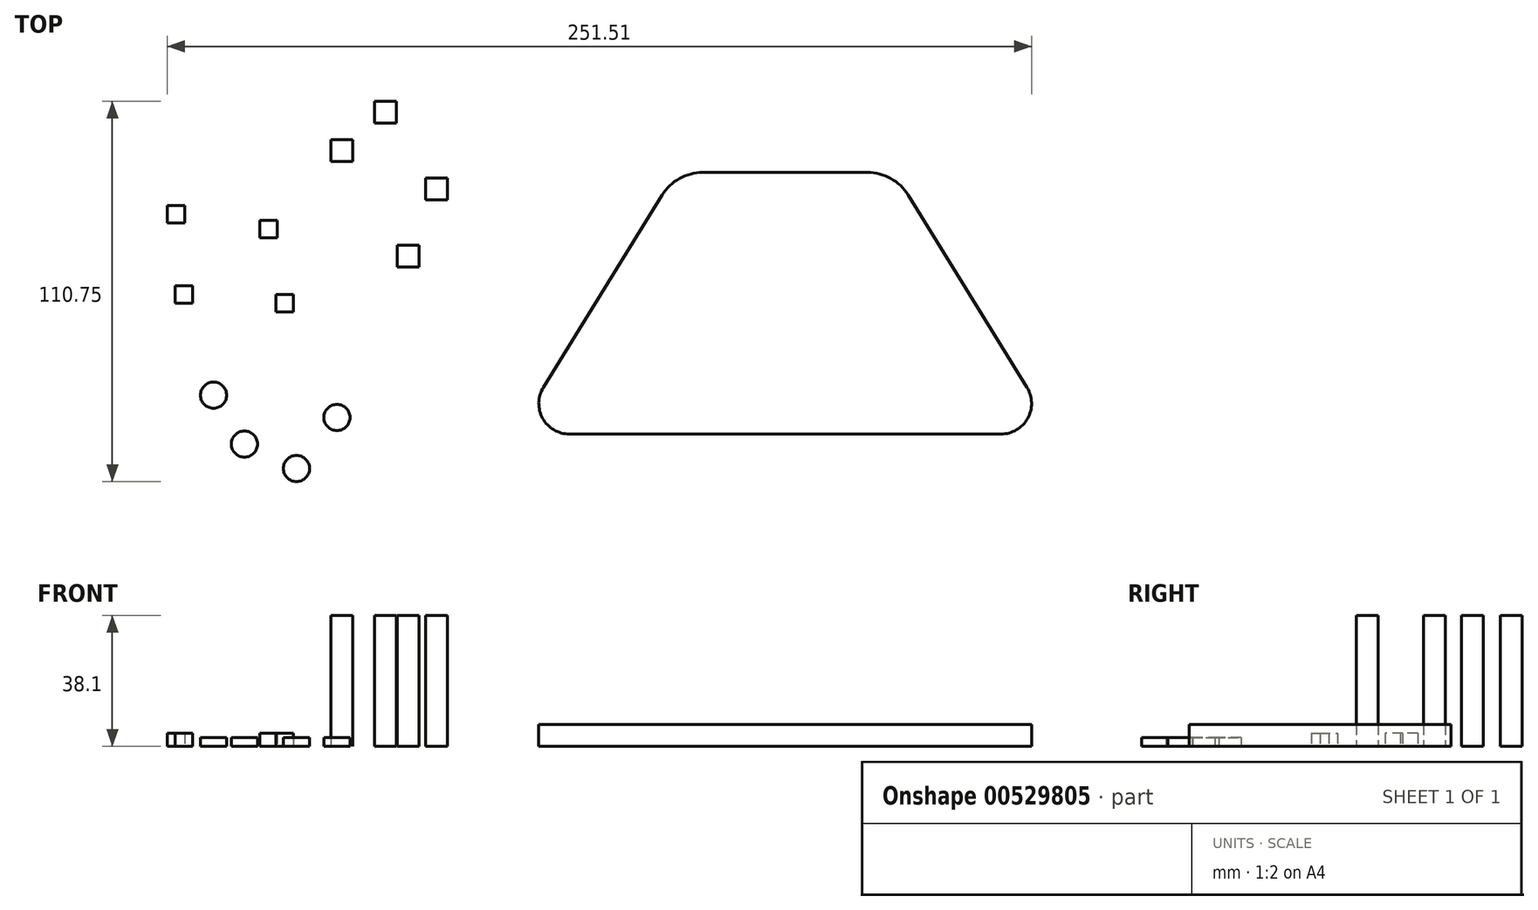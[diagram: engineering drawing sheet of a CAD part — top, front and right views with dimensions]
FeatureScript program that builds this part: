
annotation { "Feature Type Name" : "Feature", "Feature Type Description" : "" }
export const myFeature = defineFeature(function(context is Context, id is Id, definition is map)
    precondition{}
    {
        {
            var Q0;
            Q0=qCreatedBy(makeId("Top.planeOp"),FACE);
            var sketch = newSketch(context, id + "F0", { "sketchPlane" : qUnion([Q0])});
            skLineSegment(sketch, "E0.bottom", {"start": v(-23.95, 38.1) * mm, "end": v(23.95, 38.1) * mm});
            skLineSegment(sketch, "E0.top", {"start": v(-31.75, -38.1) * mm, "end": v(31.75, -38.1) * mm});
            skLineSegment(sketch, "E0.left", {"start": v(-31.75, 38.1) * mm, "end": v(-31.75, -38.1) * mm});
            skLineSegment(sketch, "E0.right", {"start": v(31.75, 38.1) * mm, "end": v(31.75, -38.1) * mm});
            skPoint(sketch, "E0.middle", {"position": v(0, 0) * mm});
            skLineSegment(sketch, "E1", {"start": v(-31.75, -38.1) * mm, "end": v(-62.81, -38.1) * mm});
            skLineSegment(sketch, "E2", {"start": v(31.75, -38.1) * mm, "end": v(62.81, -38.1) * mm});
            skLineSegment(sketch, "E3", {"start": v(-35.84, 31.46) * mm, "end": v(-70.38, -24.54) * mm});
            skLineSegment(sketch, "E4", {"start": v(35.84, 31.46) * mm, "end": v(70.38, -24.54) * mm});
            skPoint(sketch, "E5.visualSharp", {"position": v(-31.75, 38.1) * mm});
            skArc(sketch, "E5.filletArc", {"start": v(-23.95, 38.1) * mm, "mid": v(-30.76, 36.33) * mm, "end": v(-35.84, 31.46) * mm});
            skPoint(sketch, "E6.visualSharp", {"position": v(31.75, 38.1) * mm});
            skArc(sketch, "E6.filletArc", {"start": v(35.84, 31.46) * mm, "mid": v(30.76, 36.33) * mm, "end": v(23.95, 38.1) * mm});
            skPoint(sketch, "E7.visualSharp", {"position": v(-78.74, -38.1) * mm});
            skArc(sketch, "E7.filletArc", {"start": v(-70.38, -24.54) * mm, "mid": v(-70.58, -33.54) * mm, "end": v(-62.81, -38.1) * mm});
            skPoint(sketch, "E8.visualSharp", {"position": v(78.74, -38.1) * mm});
            skArc(sketch, "E8.filletArc", {"start": v(62.81, -38.1) * mm, "mid": v(70.58, -33.54) * mm, "end": v(70.38, -24.54) * mm});
            skSolve(sketch);
        }
        {
            var Q0;
            {var subQ4=sQuery(id+"F0.wireOp",EDGE,"E1");Q0=makeQuery(id+"F0.imprint","IMPRINT",FACE,{"disambiguationData":[TD([[makeQuery(id+"F0.imprint","IMPRINT",EDGE,{"derivedFrom":subQ4}),-1.0]])]});}
            var Q1;
            {var subQ7=sQuery(id+"F0.wireOp",EDGE,"E0.bottom");Q1=makeQuery(id+"F0.imprint","IMPRINT",FACE,{"disambiguationData":[TD([[makeQuery(id+"F0.imprint","IMPRINT",EDGE,{"derivedFrom":subQ7}),-1.0]])]});}
            var Q2;
            {var subQ4=sQuery(id+"F0.wireOp",EDGE,"E2");Q2=makeQuery(id+"F0.imprint","IMPRINT",FACE,{"disambiguationData":[TD([[makeQuery(id+"F0.imprint","IMPRINT",EDGE,{"derivedFrom":subQ4}),1.0]])]});}
            extrude(context, id + "F1", {"entities" : qUnion([Q0, Q1, Q2]), "depth" : 6.35 * mm, "offsetDistance" : 25.4 * mm});
        }
        {
            var Q0;
            Q0=qCreatedBy(makeId("Top.planeOp"),FACE);
            var sketch = newSketch(context, id + "F2", { "sketchPlane" : qUnion([Q0])});
            skLineSegment(sketch, "E9.bottom", {"start": v(-113.12, 52.46) * mm, "end": v(-119.47, 52.46) * mm});
            skLineSegment(sketch, "E9.top", {"start": v(-113.12, 58.81) * mm, "end": v(-119.47, 58.81) * mm});
            skLineSegment(sketch, "E9.left", {"start": v(-113.12, 52.46) * mm, "end": v(-113.12, 58.81) * mm});
            skLineSegment(sketch, "E9.right", {"start": v(-119.47, 52.46) * mm, "end": v(-119.47, 58.81) * mm});
            skPoint(sketch, "E9.middle", {"position": v(-116.3, 55.64) * mm});
            skLineSegment(sketch, "E10.bottom", {"start": v(-125.9, 41.24) * mm, "end": v(-132.24, 41.24) * mm});
            skLineSegment(sketch, "E10.top", {"start": v(-125.9, 47.6) * mm, "end": v(-132.24, 47.6) * mm});
            skLineSegment(sketch, "E10.left", {"start": v(-125.9, 41.24) * mm, "end": v(-125.9, 47.6) * mm});
            skLineSegment(sketch, "E10.right", {"start": v(-132.24, 41.24) * mm, "end": v(-132.24, 47.6) * mm});
            skPoint(sketch, "E10.middle", {"position": v(-129.07, 44.42) * mm});
            skLineSegment(sketch, "E11.bottom", {"start": v(-106.52, 10.57) * mm, "end": v(-112.87, 10.57) * mm});
            skLineSegment(sketch, "E11.top", {"start": v(-106.52, 16.92) * mm, "end": v(-112.87, 16.92) * mm});
            skLineSegment(sketch, "E11.left", {"start": v(-106.52, 10.57) * mm, "end": v(-106.52, 16.92) * mm});
            skLineSegment(sketch, "E11.right", {"start": v(-112.87, 10.57) * mm, "end": v(-112.87, 16.92) * mm});
            skPoint(sketch, "E11.middle", {"position": v(-109.7, 13.75) * mm});
            skLineSegment(sketch, "E12.bottom", {"start": v(-98.24, 30.1) * mm, "end": v(-104.6, 30.1) * mm});
            skLineSegment(sketch, "E12.top", {"start": v(-98.24, 36.44) * mm, "end": v(-104.6, 36.44) * mm});
            skLineSegment(sketch, "E12.left", {"start": v(-98.24, 30.1) * mm, "end": v(-98.24, 36.44) * mm});
            skLineSegment(sketch, "E12.right", {"start": v(-104.6, 30.1) * mm, "end": v(-104.6, 36.44) * mm});
            skPoint(sketch, "E12.middle", {"position": v(-101.42, 33.27) * mm});
            skSolve(sketch);
        }
        {
            var Q0;
            Q0=makeQuery(id+"F2.imprint","IMPRINT",FACE,{"disambiguationData":[TD([[makeQuery(id+"F2.imprint","IMPRINT",EDGE,{"derivedFrom":sQuery(id+"F2.wireOp",EDGE,"E9.bottom")}),-1.0]])]});
            var Q1;
            Q1=makeQuery(id+"F2.imprint","IMPRINT",FACE,{"disambiguationData":[TD([[makeQuery(id+"F2.imprint","IMPRINT",EDGE,{"derivedFrom":sQuery(id+"F2.wireOp",EDGE,"E11.bottom")}),-1.0]])]});
            var Q2;
            Q2=makeQuery(id+"F2.imprint","IMPRINT",FACE,{"disambiguationData":[TD([[makeQuery(id+"F2.imprint","IMPRINT",EDGE,{"derivedFrom":sQuery(id+"F2.wireOp",EDGE,"E12.bottom")}),-1.0]])]});
            var Q3;
            Q3=makeQuery(id+"F2.imprint","IMPRINT",FACE,{"disambiguationData":[TD([[makeQuery(id+"F2.imprint","IMPRINT",EDGE,{"derivedFrom":sQuery(id+"F2.wireOp",EDGE,"E10.bottom")}),-1.0]])]});
            extrude(context, id + "F3", {"entities" : qUnion([Q0, Q1, Q2, Q3]), "depth" : 38.1 * mm, "offsetDistance" : 25.4 * mm});
        }
        {
            var Q0;
            Q0=qCreatedBy(makeId("Top.planeOp"),FACE);
            var sketch = newSketch(context, id + "F4", { "sketchPlane" : qUnion([Q0])});
            skLineSegment(sketch, "E13.bottom", {"start": v(-143.1, -2.54) * mm, "end": v(-148.18, -2.54) * mm});
            skLineSegment(sketch, "E13.top", {"start": v(-143.1, 2.54) * mm, "end": v(-148.18, 2.54) * mm});
            skLineSegment(sketch, "E13.left", {"start": v(-143.1, -2.54) * mm, "end": v(-143.1, 2.54) * mm});
            skLineSegment(sketch, "E13.right", {"start": v(-148.18, -2.54) * mm, "end": v(-148.18, 2.54) * mm});
            skPoint(sketch, "E13.middle", {"position": v(-145.64, 0) * mm});
            skLineSegment(sketch, "E14.bottom", {"start": v(-177.52, 0) * mm, "end": v(-172.44, 0) * mm});
            skLineSegment(sketch, "E14.top", {"start": v(-177.52, 5.08) * mm, "end": v(-172.44, 5.08) * mm});
            skLineSegment(sketch, "E14.left", {"start": v(-177.52, 0) * mm, "end": v(-177.52, 5.08) * mm});
            skLineSegment(sketch, "E14.right", {"start": v(-172.44, 0) * mm, "end": v(-172.44, 5.08) * mm});
            skPoint(sketch, "E14.middle", {"position": v(-174.98, 2.54) * mm});
            skLineSegment(sketch, "E15.bottom", {"start": v(-152.88, 24.12) * mm, "end": v(-147.8, 24.12) * mm});
            skLineSegment(sketch, "E15.top", {"start": v(-152.88, 19.04) * mm, "end": v(-147.8, 19.04) * mm});
            skLineSegment(sketch, "E15.left", {"start": v(-152.88, 24.12) * mm, "end": v(-152.88, 19.04) * mm});
            skLineSegment(sketch, "E15.right", {"start": v(-147.8, 24.12) * mm, "end": v(-147.8, 19.04) * mm});
            skPoint(sketch, "E15.middle", {"position": v(-150.34, 21.58) * mm});
            skLineSegment(sketch, "E16.bottom", {"start": v(-179.81, 28.45) * mm, "end": v(-174.73, 28.45) * mm});
            skLineSegment(sketch, "E16.top", {"start": v(-179.81, 23.37) * mm, "end": v(-174.73, 23.37) * mm});
            skLineSegment(sketch, "E16.left", {"start": v(-179.81, 28.45) * mm, "end": v(-179.81, 23.37) * mm});
            skLineSegment(sketch, "E16.right", {"start": v(-174.73, 28.45) * mm, "end": v(-174.73, 23.37) * mm});
            skPoint(sketch, "E16.middle", {"position": v(-177.27, 25.9) * mm});
            skSolve(sketch);
        }
        {
            var Q0;
            Q0=makeQuery(id+"F4.imprint","IMPRINT",FACE,{"disambiguationData":[TD([[makeQuery(id+"F4.imprint","IMPRINT",EDGE,{"derivedFrom":sQuery(id+"F4.wireOp",EDGE,"E16.bottom")}),-1.0]])]});
            var Q1;
            Q1=makeQuery(id+"F4.imprint","IMPRINT",FACE,{"disambiguationData":[TD([[makeQuery(id+"F4.imprint","IMPRINT",EDGE,{"derivedFrom":sQuery(id+"F4.wireOp",EDGE,"E14.bottom")}),1.0]])]});
            var Q2;
            Q2=makeQuery(id+"F4.imprint","IMPRINT",FACE,{"disambiguationData":[TD([[makeQuery(id+"F4.imprint","IMPRINT",EDGE,{"derivedFrom":sQuery(id+"F4.wireOp",EDGE,"E13.bottom")}),-1.0]])]});
            var Q3;
            Q3=makeQuery(id+"F4.imprint","IMPRINT",FACE,{"disambiguationData":[TD([[makeQuery(id+"F4.imprint","IMPRINT",EDGE,{"derivedFrom":sQuery(id+"F4.wireOp",EDGE,"E15.bottom")}),-1.0]])]});
            extrude(context, id + "F5", {"entities" : qUnion([Q0, Q1, Q2, Q3]), "depth" : 3.8 * mm, "offsetDistance" : 25.4 * mm});
        }
        {
            var Q0;
            Q0=qCreatedBy(makeId("Top.planeOp"),FACE);
            var sketch = newSketch(context, id + "F6", { "sketchPlane" : qUnion([Q0])});
            skCircle(sketch, "E17", {"center": v(-142.23, -48.13) * mm, "radius": 3.81 * mm});
            skCircle(sketch, "E18", {"center": v(-166.38, -26.77) * mm, "radius": 3.81 * mm});
            skCircle(sketch, "E19", {"center": v(-130.47, -33.27) * mm, "radius": 3.81 * mm});
            skCircle(sketch, "E20", {"center": v(-157.4, -41.01) * mm, "radius": 3.81 * mm});
            skSolve(sketch);
        }
        {
            var Q0;
            Q0=makeQuery(id+"F6.imprint","IMPRINT",FACE,{"disambiguationData":[TD([[makeQuery(id+"F6.imprint","IMPRINT",EDGE,{"derivedFrom":sQuery(id+"F6.wireOp",EDGE,"E18")}),1.0]])]});
            var Q1;
            Q1=makeQuery(id+"F6.imprint","IMPRINT",FACE,{"disambiguationData":[TD([[makeQuery(id+"F6.imprint","IMPRINT",EDGE,{"derivedFrom":sQuery(id+"F6.wireOp",EDGE,"E17")}),1.0]])]});
            var Q2;
            Q2=makeQuery(id+"F6.imprint","IMPRINT",FACE,{"disambiguationData":[TD([[makeQuery(id+"F6.imprint","IMPRINT",EDGE,{"derivedFrom":sQuery(id+"F6.wireOp",EDGE,"E20")}),1.0]])]});
            var Q3;
            Q3=makeQuery(id+"F6.imprint","IMPRINT",FACE,{"disambiguationData":[TD([[makeQuery(id+"F6.imprint","IMPRINT",EDGE,{"derivedFrom":sQuery(id+"F6.wireOp",EDGE,"E19")}),1.0]])]});
            extrude(context, id + "F7", {"entities" : qUnion([Q0, Q1, Q2, Q3]), "depth" : 2.54 * mm, "offsetDistance" : 25.4 * mm});
        }
    });
